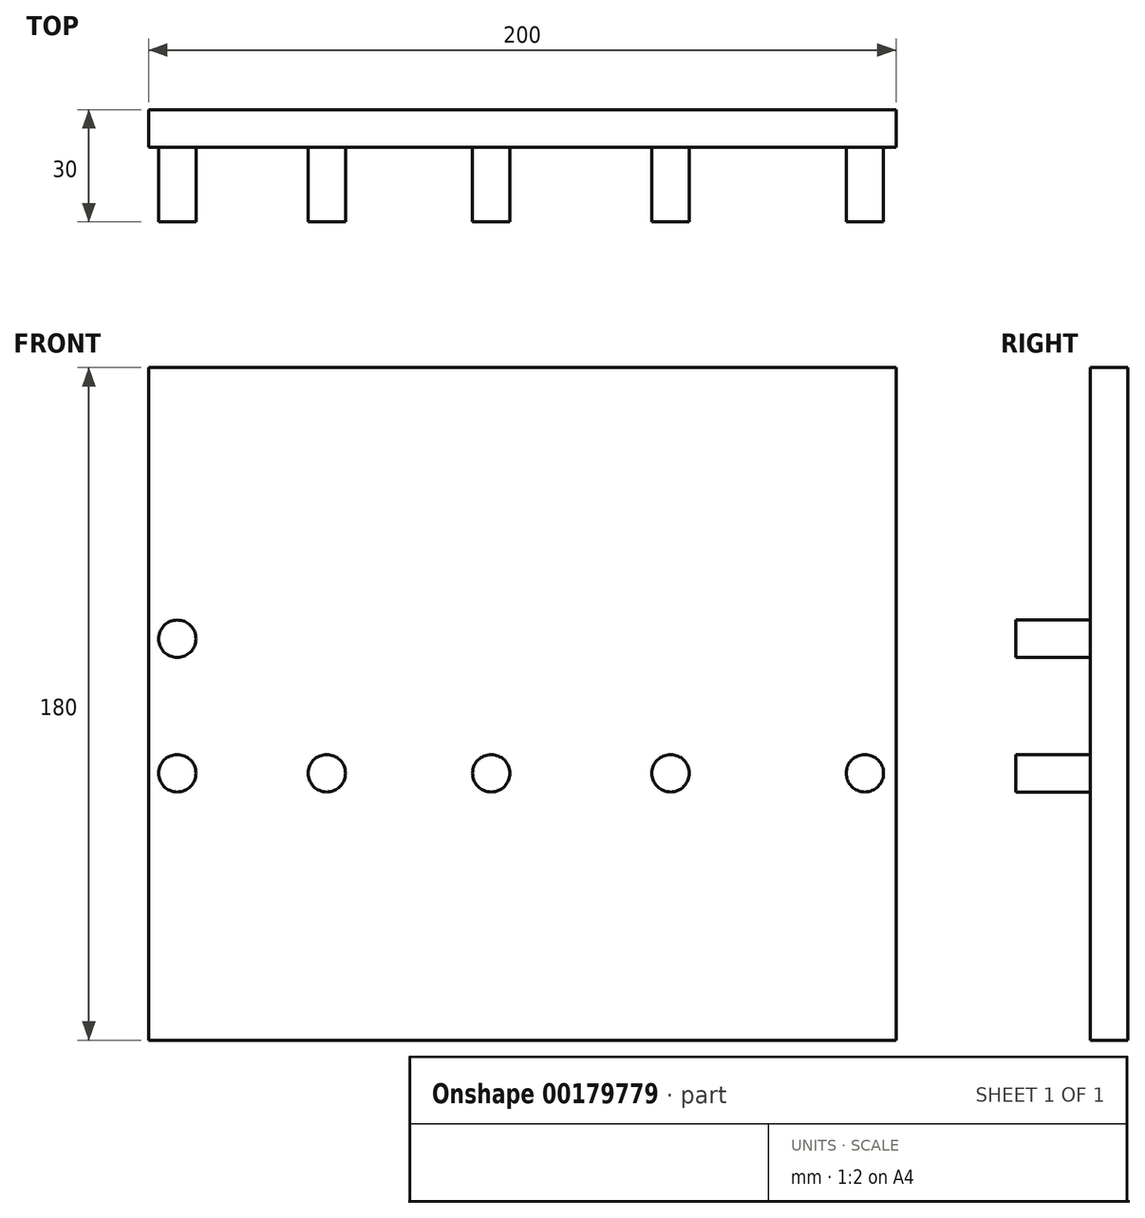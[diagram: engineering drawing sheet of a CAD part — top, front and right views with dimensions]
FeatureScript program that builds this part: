
annotation { "Feature Type Name" : "Feature", "Feature Type Description" : "" }
export const myFeature = defineFeature(function(context is Context, id is Id, definition is map)
    precondition{}
    {
        {
            var Q0;
            Q0=qCreatedBy(makeId("Front.planeOp"),FACE);
            var sketch = newSketch(context, id + "F0", { "sketchPlane" : qUnion([Q0])});
            skLineSegment(sketch, "E0.bottom", {"start": v(-242.65, 108.57) * mm, "end": v(-42.65, 108.57) * mm});
            skLineSegment(sketch, "E0.top", {"start": v(-242.65, -71.43) * mm, "end": v(-42.65, -71.43) * mm});
            skLineSegment(sketch, "E0.left", {"start": v(-242.65, 108.57) * mm, "end": v(-242.65, -71.43) * mm});
            skLineSegment(sketch, "E0.right", {"start": v(-42.65, 108.57) * mm, "end": v(-42.65, -71.43) * mm});
            skSolve(sketch);
        }
        {
            var Q0;
            Q0 = qSketchRegion(id + "F0", true);
            extrude(context, id + "F1", {"entities" : qUnion([Q0]), "depth" : 10 * mm});
        }
        {
            var Q0;
            Q0=makeQuery(id+"F1.opExtrude","CAP_FACE",FACE,{"disambiguationData":[OSD([sQuery(id+"F0.wireOp",EDGE,"E0.bottom"),sQuery(id+"F0.wireOp",EDGE,"E0.top"),sQuery(id+"F0.wireOp",EDGE,"E0.left"),sQuery(id+"F0.wireOp",EDGE,"E0.right")])],"isStart":false});
            var sketch = newSketch(context, id + "F2", { "sketchPlane" : qUnion([Q0])});
            skCircle(sketch, "E1", {"center": v(-234.98, 36) * mm, "radius": 5 * mm});
            skCircle(sketch, "E2", {"center": v(-234.98, 0) * mm, "radius": 5 * mm});
            skCircle(sketch, "E3", {"center": v(-194.98, 0) * mm, "radius": 5 * mm});
            skCircle(sketch, "E4", {"center": v(-50.98, 0) * mm, "radius": 5 * mm});
            skCircle(sketch, "E5", {"center": v(-150.98, 0) * mm, "radius": 5 * mm});
            skCircle(sketch, "E6", {"center": v(-102.98, 0) * mm, "radius": 5 * mm});
            skSolve(sketch);
        }
        {
            var Q0;
            Q0 = qSketchRegion(id + "F2", true);
            extrude(context, id + "F3", {"entities" : qUnion([Q0]), "operationType" : NewBodyOperationType.ADD, "depth" : 20 * mm});
        }
    });
